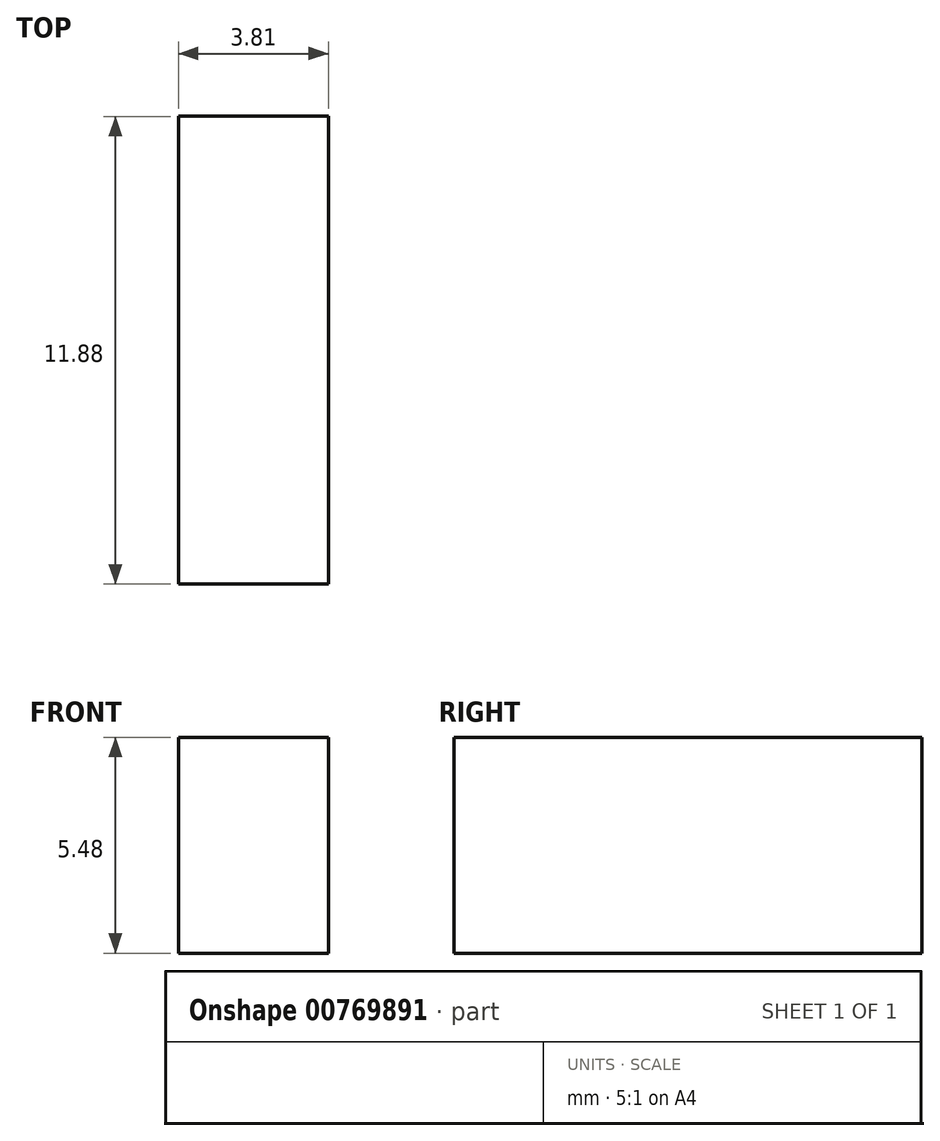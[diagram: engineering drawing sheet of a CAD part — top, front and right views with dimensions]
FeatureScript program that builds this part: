
annotation { "Feature Type Name" : "Feature", "Feature Type Description" : "" }
export const myFeature = defineFeature(function(context is Context, id is Id, definition is map)
    precondition{}
    {
        {
            var Q0;
            Q0=qCreatedBy(makeId("Right.planeOp"),FACE);
            var sketch = newSketch(context, id + "F0", { "sketchPlane" : qUnion([Q0])});
            skLineSegment(sketch, "E0.bottom", {"start": v(5.94, -2.74) * mm, "end": v(-5.94, -2.74) * mm});
            skLineSegment(sketch, "E0.top", {"start": v(5.94, 2.74) * mm, "end": v(-5.94, 2.74) * mm});
            skLineSegment(sketch, "E0.left", {"start": v(5.94, -2.74) * mm, "end": v(5.94, 2.74) * mm});
            skLineSegment(sketch, "E0.right", {"start": v(-5.94, -2.74) * mm, "end": v(-5.94, 2.74) * mm});
            skPoint(sketch, "E0.middle", {"position": v(0, 0) * mm});
            skSolve(sketch);
        }
        {
            var Q0;
            Q0 = qSketchRegion(id + "F0", true);
            extrude(context, id + "F1", {"entities" : qUnion([Q0]), "depth" : 3.8 * mm, "offsetDistance" : 25.4 * mm});
        }
    });
